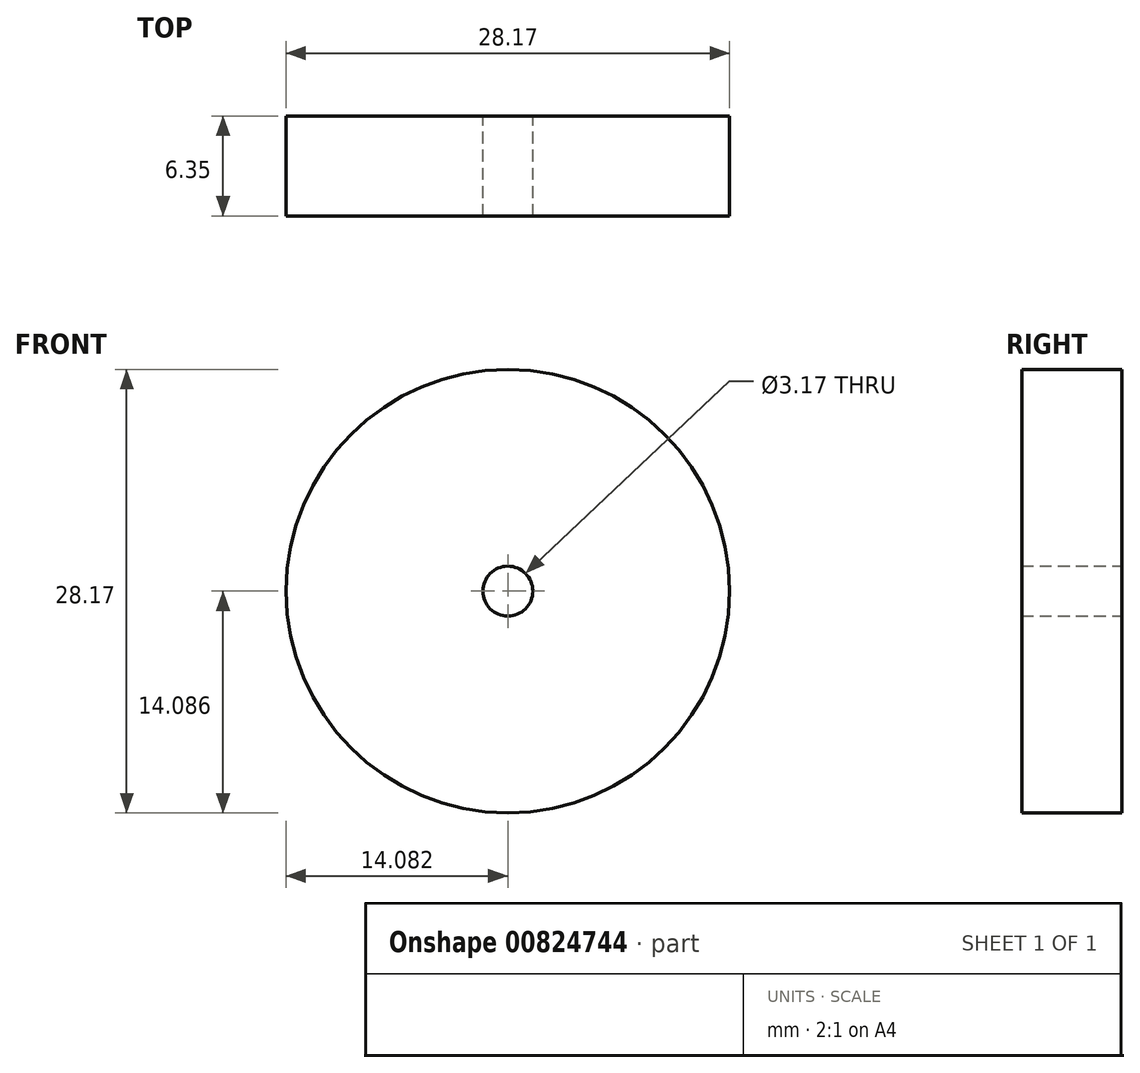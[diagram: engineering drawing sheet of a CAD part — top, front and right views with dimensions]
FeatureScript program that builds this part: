
annotation { "Feature Type Name" : "Feature", "Feature Type Description" : "" }
export const myFeature = defineFeature(function(context is Context, id is Id, definition is map)
    precondition{}
    {
        {
            var Q0;
            Q0=qCreatedBy(makeId("Front.planeOp"),FACE);
            var sketch = newSketch(context, id + "F0", { "sketchPlane" : qUnion([Q0])});
            skCircle(sketch, "E0", {"center": v(-35.2, 30.17) * mm, "radius": 14.08 * mm});
            skCircle(sketch, "E1", {"center": v(-35.2, 30.17) * mm, "radius": 1.59 * mm});
            skSolve(sketch);
        }
        {
            var Q0;
            Q0 = qSketchRegion(id + "F0", true);
            extrude(context, id + "F1", {"entities" : qUnion([Q0]), "depth" : 6.35 * mm, "offsetDistance" : 25.4 * mm});
        }
    });
